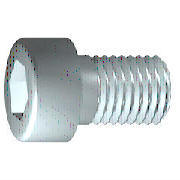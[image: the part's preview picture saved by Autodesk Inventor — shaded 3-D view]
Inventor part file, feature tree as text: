
AUTODESK INVENTOR PART (.ipt)
format: ipt  version: 2021 (Build 250183000, 183)  size: 194,048 bytes
history: native  units: mm (DEFAULTED — no unit token found)
features: sketch x2, extrude x1, plane x1, fillet x1
ambient origin geometry x7: Origin, YZ Plane, XY Plane, X Axis, Y Axis, Z Axis, Center Point
bodies: Solid1 (feature_tree), Body (feature_tree)
feature tree (5):
  extrude  "Slot"  Depth=12.0mm
  plane  "Work Plane1"
  fillet  "Fillet2"  Radius=12.0mm
  sketch  "Sketch1"  dims[d1=25.625mm d2=1.073638mm d3=12.0mm]
  sketch  "Sketch2"  dims[d4=6.0mm d5=60.0deg d6=12.0mm d7=12.0mm d8=11.547005mm d9=18.0mm d10=90.0deg d11=10.0mm d12=0.0mm d13=25.625mm d14=0.0mm d15=1.073538mm d16=1.073538mm d17=1.2mm d19=0.0mm d26=30.0mm d27=45.0deg d28=0.0mm d29=0.0mm d30=0.1mm]
